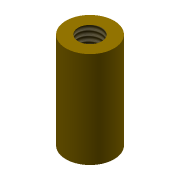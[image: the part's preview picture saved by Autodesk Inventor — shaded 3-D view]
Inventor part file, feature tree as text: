
AUTODESK INVENTOR PART (.ipt)
format: ipt  version: 2022 (Build 260153000, 153)  size: 79,360 bytes
history: native  units: mm
features: sketch x2, extrude x1, hole x1
ambient origin geometry x8: Origin, YZ Plane, XZ Plane, XY Plane, X Axis, Y Axis, Z Axis, Center Point
bodies: Solid1 (feature_tree)
feature tree (4):
  extrude  "Extrusion1"  Depth=10.0mm TaperAngle=0.0deg
  hole  "Hole1"  [1 undecoded]
  sketch  "Sketch1"  dims[d0=5.0mm d1=10.0mm d2=0.0mm]
  sketch  "Sketch2"  dims[d3=2.459mm d4=10.0mm d5=4.0mm d6=2.0mm d7=90.0deg d8=8.0mm d9=20.594885mm]
note: 1 required parameter value undecoded (feature->parameter linkage not recoverable at this tier; creation-order binding heuristic only, values carry confidence <= 0.55)
